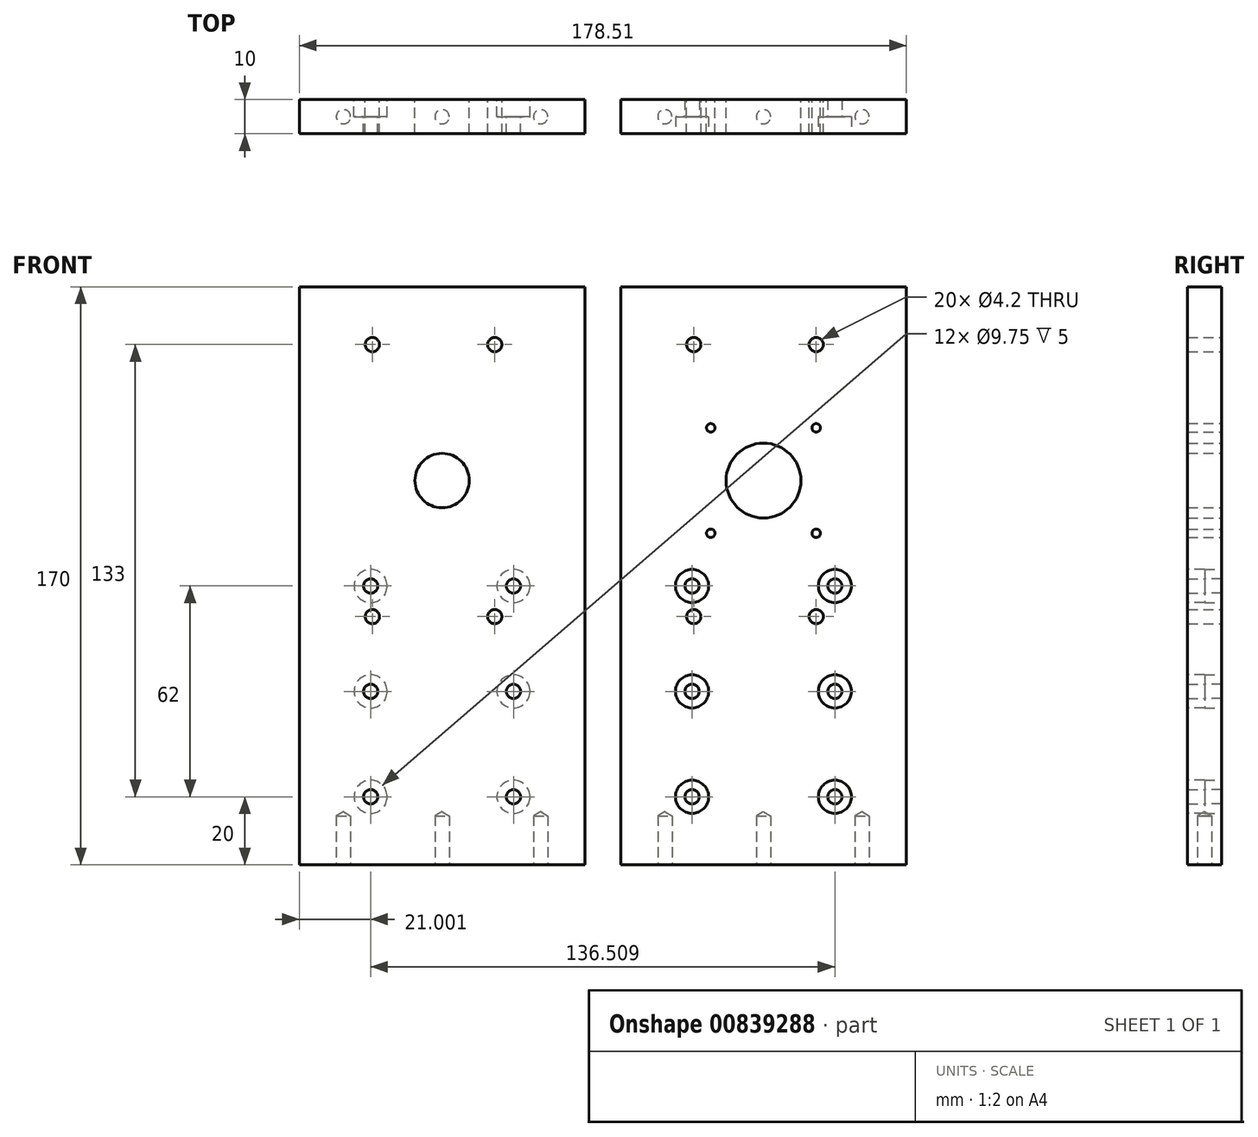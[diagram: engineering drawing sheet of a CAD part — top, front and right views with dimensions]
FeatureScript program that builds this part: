
annotation { "Feature Type Name" : "Feature", "Feature Type Description" : "" }
export const myFeature = defineFeature(function(context is Context, id is Id, definition is map)
    precondition{}
    {
        {
            var Q0;
            Q0=qCreatedBy(makeId("Front.planeOp"),FACE);
            var sketch = newSketch(context, id + "F0", { "sketchPlane" : qUnion([Q0])});
            skLineSegment(sketch, "E0.bottom", {"start": v(-42, 85) * mm, "end": v(42, 85) * mm});
            skLineSegment(sketch, "E0.top", {"start": v(-42, -85) * mm, "end": v(42, -85) * mm});
            skLineSegment(sketch, "E0.left", {"start": v(-42, 85) * mm, "end": v(-42, -85) * mm});
            skLineSegment(sketch, "E0.right", {"start": v(42, 85) * mm, "end": v(42, -85) * mm});
            skPoint(sketch, "E0.middle", {"position": v(0, 0) * mm});
            skSolve(sketch);
        }
        {
            var Q0;
            Q0=makeQuery(id+"F0.imprint","IMPRINT",FACE,{"disambiguationData":[TD([[makeQuery(id+"F0.imprint","IMPRINT",EDGE,{"derivedFrom":sQuery(id+"F0.wireOp",EDGE,"E0.bottom")}),-1.0]])]});
            extrude(context, id + "F1", {"entities" : qUnion([Q0]), "depth" : 10 * mm, "offsetDistance" : 25 * mm});
        }
        {
            var Q0;
            Q0=makeQuery(id+"F1.opExtrude","CAP_FACE",FACE,{"disambiguationData":[OSD([sQuery(id+"F0.wireOp",EDGE,"E0.bottom"),sQuery(id+"F0.wireOp",EDGE,"E0.top"),sQuery(id+"F0.wireOp",EDGE,"E0.left"),sQuery(id+"F0.wireOp",EDGE,"E0.right")])],"isStart":true});
            var sketch = newSketch(context, id + "F2", { "sketchPlane" : qUnion([Q0])});
            skCircle(sketch, "E1", {"center": v(2.5, 50) * mm, "radius": 6 * mm});
            skCircle(sketch, "E2.MirrorC", {"center": v(2.5, -50) * mm, "radius": 6 * mm});
            skPoint(sketch, "E3", {"position": v(20.5, 50) * mm});
            skPoint(sketch, "E4", {"position": v(-15.5, 50) * mm});
            skPoint(sketch, "E5.MirrorP", {"position": v(20.5, -50) * mm});
            skPoint(sketch, "E6.MirrorP", {"position": v(-15.5, -50) * mm});
            skPoint(sketch, "E7", {"position": v(20.5, -12) * mm});
            skPoint(sketch, "E8", {"position": v(-15.5, -12) * mm});
            skCircle(sketch, "E9", {"center": v(0, 28) * mm, "radius": 11 * mm});
            skPoint(sketch, "E10", {"position": v(-15.5, 43.5) * mm});
            skLineSegment(sketch, "E11", {"start": v(0, 28) * mm, "end": v(0, 33.72) * mm});
            skPoint(sketch, "E12.MirrorP", {"position": v(15.5, 43.5) * mm});
            skLineSegment(sketch, "E13", {"start": v(0, 28) * mm, "end": v(2.49, 28) * mm});
            skPoint(sketch, "E14.MirrorP", {"position": v(15.5, 12.5) * mm});
            skPoint(sketch, "E15.MirrorP", {"position": v(-15.5, 12.5) * mm});
            skPoint(sketch, "E16.MirrorP", {"position": v(-15.5, 68) * mm});
            skPoint(sketch, "E17.MirrorP", {"position": v(20.5, 68) * mm});
            skSolve(sketch);
        }
        {
            var Q0;
            Q0=makeQuery(id+"F1.opExtrude","SWEPT_FACE",FACE,{"disambiguationData":[OSD([sQuery(id+"F0.wireOp",EDGE,"E0.top")])]});
            var sketch = newSketch(context, id + "F3", { "sketchPlane" : qUnion([Q0])});
            skPoint(sketch, "E18", {"position": v(0, 5) * mm});
            skPoint(sketch, "E18.positionSnap0", {"position": v(0, 0) * mm});
            skPoint(sketch, "E19", {"position": v(29, 5) * mm});
            skPoint(sketch, "E20.MirrorP", {"position": v(-29, 5) * mm});
            skSolve(sketch);
        }
        {
            var Q0;
            Q0=sQuery(id+"F3.wireOp",VERTEX,"E20.MirrorP");
            var Q1;
            Q1=sQuery(id+"F3.wireOp",VERTEX,"E18");
            var Q2;
            Q2=sQuery(id+"F3.wireOp",VERTEX,"E19");
            var Q3;
            Q3=makeQuery(id+"F1.opExtrude","SWEPT_BODY",BODY,{"disambiguationData":[OSD([sQuery(id+"F0.wireOp",EDGE,"E0.bottom"),sQuery(id+"F0.wireOp",EDGE,"E0.top"),sQuery(id+"F0.wireOp",EDGE,"E0.left"),sQuery(id+"F0.wireOp",EDGE,"E0.right")])]});
            hole(context, id + "F4", {"style" : HoleStyle.SIMPLE, "endStyle" : HoleEndStyle.BLIND, "standardTappedOrClearance" : lookupTablePath({ "standard" : "ISO", "engagement" : "75%", "pitch" : "0.8 mm", "size" : "M5", "type" : "Tapped" }), "standardBlindInLast" : lookupTablePath({ "standard" : "ISO", "fit" : "Normal", "engagement" : "75%", "pitch" : "0.8 mm", "size" : "M5", "type" : "Clearance & tapped" }), "holeDiameter" : 4.2 * mm, "majorDiameter" : 5 * mm, "showTappedDepth" : true, "holeDepth" : 14.4 * mm, "isTappedThrough" : true, "tappedDepth" : 12 * mm, "tapClearance" : 3, "locations" : qUnion([Q0, Q1, Q2]), "scope" : qUnion([Q3])});
        }
        {
            var Q0;
            Q0=qCreatedBy(makeId("Front.planeOp"),FACE);
            var sketch = newSketch(context, id + "F5", { "sketchPlane" : qUnion([Q0])});
            skLineSegment(sketch, "E21.bottom", {"start": v(-136.5, 85) * mm, "end": v(-52.5, 85) * mm});
            skLineSegment(sketch, "E21.top", {"start": v(-136.5, -85) * mm, "end": v(-52.5, -85) * mm});
            skLineSegment(sketch, "E21.left", {"start": v(-136.5, 85) * mm, "end": v(-136.5, -85) * mm});
            skLineSegment(sketch, "E21.right", {"start": v(-52.5, 85) * mm, "end": v(-52.5, -85) * mm});
            skPoint(sketch, "E21.middle", {"position": v(-94.5, 0) * mm});
            skCircle(sketch, "E22", {"center": v(-94.5, 0) * mm, "radius": 8 * mm});
            skPoint(sketch, "E23", {"position": v(-78.15, -12) * mm});
            skCircle(sketch, "E24", {"center": v(-94.5, 28) * mm, "radius": 8 * mm});
            skSolve(sketch);
        }
        {
            var Q0;
            Q0=makeQuery(id+"F5.imprint","IMPRINT",FACE,{"disambiguationData":[TD([[makeQuery(id+"F5.imprint","IMPRINT",EDGE,{"derivedFrom":sQuery(id+"F5.wireOp",EDGE,"E21.bottom")}),-1.0]])]});
            var Q1;
            Q1=makeQuery(id+"F5.imprint","IMPRINT",FACE,{"disambiguationData":[TD([[makeQuery(id+"F5.imprint","IMPRINT",EDGE,{"derivedFrom":sQuery(id+"F5.wireOp",EDGE,"E22")}),1.0]])]});
            extrude(context, id + "F6", {"entities" : qUnion([Q0, Q1]), "depth" : 10 * mm, "offsetDistance" : 25 * mm});
        }
        {
            var Q0;
            Q0=makeQuery(id+"F6.opExtrude","SWEPT_FACE",FACE,{"disambiguationData":[OSD([sQuery(id+"F5.wireOp",EDGE,"E21.top")])]});
            var sketch = newSketch(context, id + "F7", { "sketchPlane" : qUnion([Q0])});
            skPoint(sketch, "E25", {"position": v(-94.5, 5) * mm});
            skPoint(sketch, "E25.positionSnap0", {"position": v(-94.5, 0) * mm});
            skPoint(sketch, "E26", {"position": v(-65.5, 5) * mm});
            skPoint(sketch, "E27", {"position": v(-123.5, 5) * mm});
            skSolve(sketch);
        }
        {
            var Q0;
            Q0=sQuery(id+"F7.wireOp",VERTEX,"E27");
            var Q1;
            Q1=sQuery(id+"F7.wireOp",VERTEX,"E25");
            var Q2;
            Q2=sQuery(id+"F7.wireOp",VERTEX,"E26");
            var Q3;
            Q3=makeQuery(id+"F6.opExtrude","SWEPT_BODY",BODY,{"disambiguationData":[OSD([sQuery(id+"F5.wireOp",EDGE,"E21.bottom"),sQuery(id+"F5.wireOp",EDGE,"E21.top"),sQuery(id+"F5.wireOp",EDGE,"E21.left"),sQuery(id+"F5.wireOp",EDGE,"E21.right"),sQuery(id+"F5.wireOp",EDGE,"E22"),sQuery(id+"F5.wireOp",EDGE,"VNLAGBib-wfs1-WRSX-g96t-QBW1bBah4SJk"),sQuery(id+"F5.wireOp",EDGE,"e6dab01b-e578-4f8a-8e6f-54719c1135b30.MirrorC")])]});
            hole(context, id + "F8", {"style" : HoleStyle.SIMPLE, "endStyle" : HoleEndStyle.BLIND, "standardTappedOrClearance" : lookupTablePath({ "standard" : "ISO", "engagement" : "75%", "pitch" : "0.8 mm", "size" : "M5", "type" : "Tapped" }), "standardBlindInLast" : lookupTablePath({ "standard" : "ISO", "fit" : "Normal", "engagement" : "75%", "pitch" : "0.8 mm", "size" : "M5", "type" : "Clearance & tapped" }), "holeDiameter" : 4.2 * mm, "majorDiameter" : 5 * mm, "showTappedDepth" : true, "holeDepth" : 14.4 * mm, "isTappedThrough" : true, "tappedDepth" : 12 * mm, "tapClearance" : 3, "locations" : qUnion([Q0, Q1, Q2]), "scope" : qUnion([Q3])});
        }
        {
            var Q0;
            Q0=makeQuery(id+"F6.opExtrude","CAP_FACE",FACE,{"disambiguationData":[OSD([sQuery(id+"F5.wireOp",EDGE,"E21.bottom"),sQuery(id+"F5.wireOp",EDGE,"E21.top"),sQuery(id+"F5.wireOp",EDGE,"E21.left"),sQuery(id+"F5.wireOp",EDGE,"E21.right"),sQuery(id+"F5.wireOp",EDGE,"E22")])],"isStart":true});
            var sketch = newSketch(context, id + "F9", { "sketchPlane" : qUnion([Q0])});
            skPoint(sketch, "E28", {"position": v(94.5, 50) * mm});
            skPoint(sketch, "E29", {"position": v(97, 50) * mm});
            skPoint(sketch, "E30", {"position": v(115, 50) * mm});
            skPoint(sketch, "E31", {"position": v(79, 50) * mm});
            skPoint(sketch, "E32.MirrorP", {"position": v(115, -49) * mm});
            skPoint(sketch, "E33.MirrorP", {"position": v(79, -49) * mm});
            skPoint(sketch, "E34", {"position": v(115, -12) * mm});
            skPoint(sketch, "E35", {"position": v(79, -12) * mm});
            skLineSegment(sketch, "E36", {"start": v(94.5, 28) * mm, "end": v(115, 28) * mm});
            skPoint(sketch, "E37.MirrorP", {"position": v(79, 68) * mm});
            skPoint(sketch, "E38.MirrorP", {"position": v(115, 68) * mm});
            skSolve(sketch);
        }
        {
            var Q0;
            Q0=sQuery(id+"F9.wireOp",VERTEX,"E35");
            var Q1;
            Q1=sQuery(id+"F9.wireOp",VERTEX,"E34");
            var Q2;
            Q2=sQuery(id+"F9.wireOp",VERTEX,"E37.MirrorP");
            var Q3;
            Q3=sQuery(id+"F9.wireOp",VERTEX,"E38.MirrorP");
            var Q4;
            Q4=makeQuery(id+"F6.opExtrude","SWEPT_BODY",BODY,{"disambiguationData":[OSD([sQuery(id+"F5.wireOp",EDGE,"E21.bottom"),sQuery(id+"F5.wireOp",EDGE,"E21.top"),sQuery(id+"F5.wireOp",EDGE,"E21.left"),sQuery(id+"F5.wireOp",EDGE,"E21.right"),sQuery(id+"F5.wireOp",EDGE,"E22")])]});
            hole(context, id + "F10", {"style" : HoleStyle.SIMPLE, "endStyle" : HoleEndStyle.THROUGH, "standardTappedOrClearance" : lookupTablePath({ "standard" : "ISO", "engagement" : "75%", "pitch" : "0.8 mm", "size" : "M5", "type" : "Tapped" }), "standardBlindInLast" : lookupTablePath({ "standard" : "ISO", "fit" : "Normal", "engagement" : "75%", "pitch" : "0.8 mm", "size" : "M5", "type" : "Clearance & tapped" }), "holeDiameter" : 4.2 * mm, "majorDiameter" : 5 * mm, "showTappedDepth" : true, "isTappedThrough" : true, "tappedDepth" : 10 * mm, "tapClearance" : 3, "locations" : qUnion([Q0, Q1, Q2, Q3]), "scope" : qUnion([Q4])});
        }
        {
            var Q0;
            Q0=makeQuery(id+"F1.opExtrude","CAP_FACE",FACE,{"disambiguationData":[OSD([sQuery(id+"F0.wireOp",EDGE,"E0.bottom"),sQuery(id+"F0.wireOp",EDGE,"E0.top"),sQuery(id+"F0.wireOp",EDGE,"E0.left"),sQuery(id+"F0.wireOp",EDGE,"E0.right")])],"isStart":false});
            var sketch = newSketch(context, id + "F11", { "sketchPlane" : qUnion([Q0])});
            skPoint(sketch, "E39", {"position": v(0, -65) * mm});
            skPoint(sketch, "E40", {"position": v(21, -65) * mm});
            skPoint(sketch, "E41.MirrorP", {"position": v(-21, -65) * mm});
            skPoint(sketch, "E42", {"position": v(-21, -3) * mm});
            skPoint(sketch, "E43", {"position": v(21, -3) * mm});
            skPoint(sketch, "E44", {"position": v(-21, -34) * mm});
            skPoint(sketch, "E45", {"position": v(21, -34) * mm});
            skSolve(sketch);
        }
        {
            var Q0;
            Q0=sQuery(id+"F11.wireOp",VERTEX,"E41.MirrorP");
            var Q1;
            Q1=sQuery(id+"F11.wireOp",VERTEX,"E40");
            var Q2;
            Q2=sQuery(id+"F11.wireOp",VERTEX,"E43");
            var Q3;
            Q3=sQuery(id+"F11.wireOp",VERTEX,"E42");
            var Q4;
            Q4=sQuery(id+"F11.wireOp",VERTEX,"E44");
            var Q5;
            Q5=sQuery(id+"F11.wireOp",VERTEX,"E45");
            var Q6;
            Q6=makeQuery(id+"F1.opExtrude","SWEPT_BODY",BODY,{"disambiguationData":[OSD([sQuery(id+"F0.wireOp",EDGE,"E0.bottom"),sQuery(id+"F0.wireOp",EDGE,"E0.top"),sQuery(id+"F0.wireOp",EDGE,"E0.left"),sQuery(id+"F0.wireOp",EDGE,"E0.right")])]});
            hole(context, id + "F12", {"style" : HoleStyle.C_BORE, "endStyle" : HoleEndStyle.THROUGH, "standardTappedOrClearance" : lookupTablePath({ "standard" : "ISO", "engagement" : "75%", "pitch" : "0.8 mm", "size" : "M5", "type" : "Tapped" }), "standardBlindInLast" : lookupTablePath({ "standard" : "ISO", "fit" : "Normal", "engagement" : "75%", "pitch" : "0.8 mm", "size" : "M5", "type" : "Clearance & tapped" }), "holeDiameter" : 4.2 * mm, "cBoreDiameter" : 9.75 * mm, "cBoreDepth" : 5 * mm, "majorDiameter" : 5 * mm, "showTappedDepth" : true, "isTappedThrough" : true, "tappedDepth" : 10 * mm, "tapClearance" : 3, "locations" : qUnion([Q0, Q1, Q2, Q3, Q4, Q5]), "scope" : qUnion([Q6])});
        }
        {
            var Q0;
            Q0=makeQuery(id+"F6.opExtrude","CAP_FACE",FACE,{"disambiguationData":[OSD([sQuery(id+"F5.wireOp",EDGE,"E21.bottom"),sQuery(id+"F5.wireOp",EDGE,"E21.top"),sQuery(id+"F5.wireOp",EDGE,"E21.left"),sQuery(id+"F5.wireOp",EDGE,"E21.right"),sQuery(id+"F5.wireOp",EDGE,"E22")])],"isStart":true});
            var sketch = newSketch(context, id + "F13", { "sketchPlane" : qUnion([Q0])});
            skPoint(sketch, "E46", {"position": v(73.5, -65) * mm});
            skLineSegment(sketch, "E47", {"start": v(94.5, -85) * mm, "end": v(94.5, -45.56) * mm});
            skPoint(sketch, "E48.MirrorP", {"position": v(115.5, -65) * mm});
            skPoint(sketch, "E49", {"position": v(73.5, -3) * mm});
            skPoint(sketch, "E50.MirrorP", {"position": v(115.5, -3) * mm});
            skPoint(sketch, "E51", {"position": v(73.5, -34) * mm});
            skPoint(sketch, "E52", {"position": v(115.5, -34) * mm});
            skSolve(sketch);
        }
        {
            var Q0;
            Q0=sQuery(id+"F13.wireOp",VERTEX,"E49");
            var Q1;
            Q1=sQuery(id+"F13.wireOp",VERTEX,"E50.MirrorP");
            var Q2;
            Q2=sQuery(id+"F13.wireOp",VERTEX,"E48.MirrorP");
            var Q3;
            Q3=sQuery(id+"F13.wireOp",VERTEX,"E46");
            var Q4;
            Q4=sQuery(id+"F13.wireOp",VERTEX,"E51");
            var Q5;
            Q5=sQuery(id+"F13.wireOp",VERTEX,"E52");
            var Q6;
            Q6=makeQuery(id+"F6.opExtrude","SWEPT_BODY",BODY,{"disambiguationData":[OSD([sQuery(id+"F5.wireOp",EDGE,"E21.bottom"),sQuery(id+"F5.wireOp",EDGE,"E21.top"),sQuery(id+"F5.wireOp",EDGE,"E21.left"),sQuery(id+"F5.wireOp",EDGE,"E21.right"),sQuery(id+"F5.wireOp",EDGE,"E22")])]});
            hole(context, id + "F14", {"style" : HoleStyle.C_BORE, "endStyle" : HoleEndStyle.THROUGH, "standardTappedOrClearance" : lookupTablePath({ "standard" : "ISO", "engagement" : "75%", "pitch" : "0.8 mm", "size" : "M5", "type" : "Tapped" }), "standardBlindInLast" : lookupTablePath({ "standard" : "ISO", "fit" : "Normal", "engagement" : "75%", "pitch" : "0.8 mm", "size" : "M5", "type" : "Clearance & tapped" }), "holeDiameter" : 4.2 * mm, "cBoreDiameter" : 9.75 * mm, "cBoreDepth" : 5 * mm, "majorDiameter" : 5 * mm, "showTappedDepth" : true, "isTappedThrough" : true, "tappedDepth" : 10 * mm, "tapClearance" : 3, "locations" : qUnion([Q0, Q1, Q2, Q3, Q4, Q5]), "scope" : qUnion([Q6])});
        }
        {
            var Q0;
            Q0=makeQuery(id+"F2.imprint","IMPRINT",FACE,{"disambiguationData":[TD([[makeQuery(id+"F2.imprint","IMPRINT",EDGE,{"derivedFrom":sQuery(id+"F2.wireOp",EDGE,"E9")}),1.0]])]});
            extrude(context, id + "F15", {"entities" : qUnion([Q0]), "operationType" : NewBodyOperationType.REMOVE, "oppositeDirection" : true, "depth" : 25 * mm, "offsetDistance" : 25 * mm});
        }
        {
            var Q0;
            Q0=sQuery(id+"F2.wireOp",VERTEX,"E16.MirrorP");
            var Q1;
            Q1=sQuery(id+"F2.wireOp",VERTEX,"E17.MirrorP");
            var Q2;
            Q2=sQuery(id+"F2.wireOp",VERTEX,"E8");
            var Q3;
            Q3=sQuery(id+"F2.wireOp",VERTEX,"E7");
            var Q4;
            Q4=makeQuery(id+"F1.opExtrude","SWEPT_BODY",BODY,{"disambiguationData":[OSD([sQuery(id+"F0.wireOp",EDGE,"E0.bottom"),sQuery(id+"F0.wireOp",EDGE,"E0.top"),sQuery(id+"F0.wireOp",EDGE,"E0.left"),sQuery(id+"F0.wireOp",EDGE,"E0.right")])]});
            hole(context, id + "F16", {"style" : HoleStyle.SIMPLE, "endStyle" : HoleEndStyle.THROUGH, "standardTappedOrClearance" : lookupTablePath({ "standard" : "ISO", "engagement" : "75%", "pitch" : "0.8 mm", "size" : "M5", "type" : "Tapped" }), "standardBlindInLast" : lookupTablePath({ "standard" : "ISO", "fit" : "Normal", "engagement" : "75%", "pitch" : "0.8 mm", "size" : "M5", "type" : "Clearance & tapped" }), "holeDiameter" : 4.2 * mm, "majorDiameter" : 5 * mm, "showTappedDepth" : true, "isTappedThrough" : true, "tappedDepth" : 10 * mm, "tapClearance" : 3, "locations" : qUnion([Q0, Q1, Q2, Q3]), "scope" : qUnion([Q4])});
        }
        {
            var Q0;
            Q0=sQuery(id+"F2.wireOp",VERTEX,"E10");
            var Q1;
            Q1=sQuery(id+"F2.wireOp",VERTEX,"E12.MirrorP");
            var Q2;
            Q2=sQuery(id+"F2.wireOp",VERTEX,"E15.MirrorP");
            var Q3;
            Q3=sQuery(id+"F2.wireOp",VERTEX,"E14.MirrorP");
            var Q4;
            Q4=makeQuery(id+"F1.opExtrude","SWEPT_BODY",BODY,{"disambiguationData":[OSD([sQuery(id+"F0.wireOp",EDGE,"E0.bottom"),sQuery(id+"F0.wireOp",EDGE,"E0.top"),sQuery(id+"F0.wireOp",EDGE,"E0.left"),sQuery(id+"F0.wireOp",EDGE,"E0.right")])]});
            hole(context, id + "F17", {"style" : HoleStyle.SIMPLE, "endStyle" : HoleEndStyle.THROUGH, "standardTappedOrClearance" : lookupTablePath({ "standard" : "ISO", "engagement" : "75%", "pitch" : "0.5 mm", "size" : "M3", "type" : "Tapped" }), "standardBlindInLast" : lookupTablePath({ "standard" : "ISO", "fit" : "Normal", "engagement" : "75%", "pitch" : "0.5 mm", "size" : "M3", "type" : "Clearance & tapped" }), "holeDiameter" : 2.5 * mm, "majorDiameter" : 3 * mm, "showTappedDepth" : true, "isTappedThrough" : true, "tappedDepth" : 10 * mm, "tapClearance" : 3, "locations" : qUnion([Q0, Q1, Q2, Q3]), "scope" : qUnion([Q4])});
        }
    });
